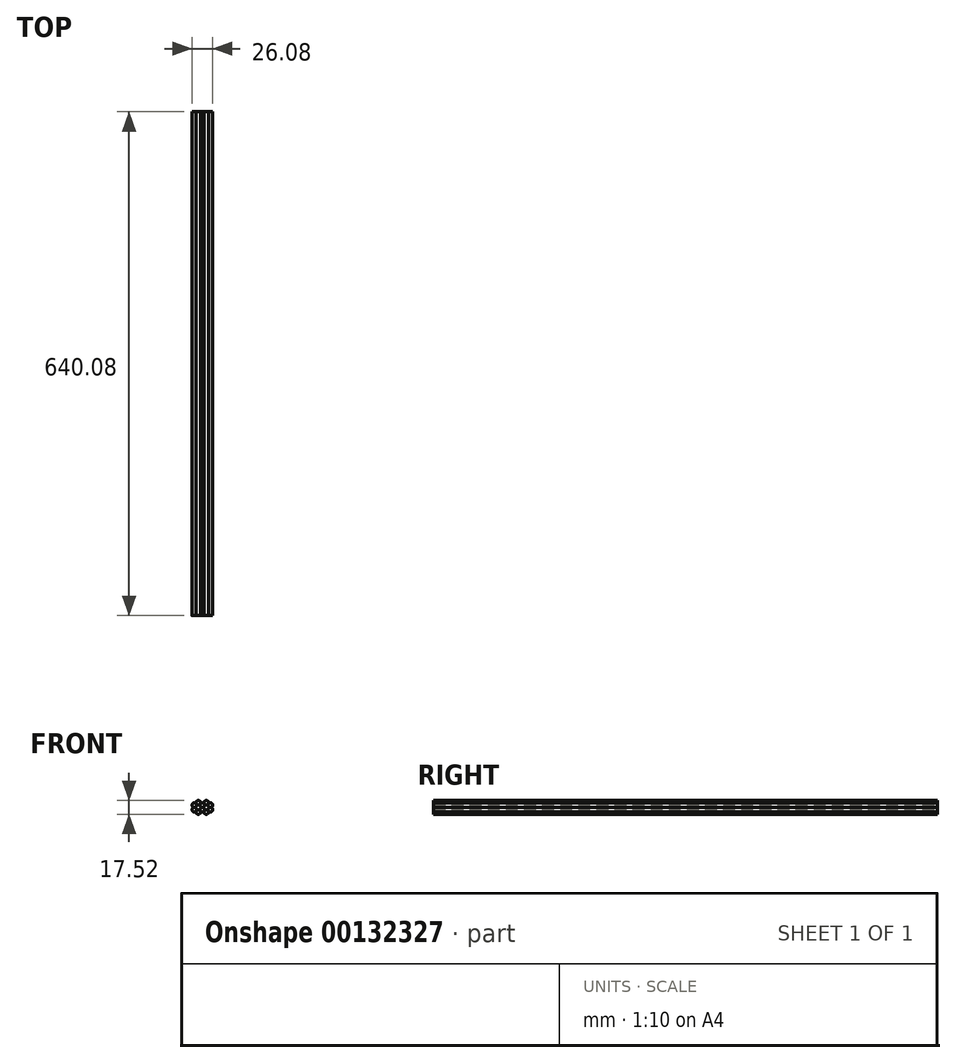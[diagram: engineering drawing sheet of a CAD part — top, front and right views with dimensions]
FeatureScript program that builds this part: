
annotation { "Feature Type Name" : "Feature", "Feature Type Description" : "" }
export const myFeature = defineFeature(function(context is Context, id is Id, definition is map)
    precondition{}
    {
        {
            var Q0;
            Q0=qCreatedBy(makeId("Front.planeOp"),FACE);
            var sketch = newSketch(context, id + "F0", { "sketchPlane" : qUnion([Q0])});
            skCircle(sketch, "E0", {"center": v(0, 0) * mm, "radius": 2.92 * mm});
            skCircle(sketch, "E1", {"center": v(-5.06, 2.92) * mm, "radius": 2.92 * mm});
            skCircle(sketch, "E2", {"center": v(-10.12, 0) * mm, "radius": 2.92 * mm});
            skCircle(sketch, "E3", {"center": v(-10.12, -5.84) * mm, "radius": 2.92 * mm});
            skCircle(sketch, "E4", {"center": v(-5.06, -8.76) * mm, "radius": 2.92 * mm});
            skCircle(sketch, "E5", {"center": v(5.06, 2.92) * mm, "radius": 2.92 * mm});
            skCircle(sketch, "E6", {"center": v(10.12, 0) * mm, "radius": 2.92 * mm});
            skCircle(sketch, "E7", {"center": v(10.12, -5.84) * mm, "radius": 2.92 * mm});
            skCircle(sketch, "E8", {"center": v(5.06, -8.76) * mm, "radius": 2.92 * mm});
            skCircle(sketch, "E9", {"center": v(0, -5.84) * mm, "radius": 2.92 * mm});
            skSolve(sketch);
        }
        {
            var Q0;
            {var subQ0=sQuery(id+"F0.wireOp",EDGE,"E8");var subQ1=makeQuery(id+"F0.imprint","INTERSECT",VERTEX,{"derivedFrom":[sQuery(id+"F0.wireOp",EDGE,"E7"),subQ0]});Q0=makeQuery(id+"F0.imprint","IMPRINT",FACE,{"disambiguationData":[TD([[makeQuery(id+"F0.imprint","IMPRINT",EDGE,{"disambiguationData":[TD([[subQ1,-1.0]])],"derivedFrom":subQ0}),1.0]])]});}
            var Q1;
            {var subQ0=sQuery(id+"F0.wireOp",EDGE,"E0");var subQ1=makeQuery(id+"F0.imprint","INTERSECT",VERTEX,{"derivedFrom":[subQ0,sQuery(id+"F0.wireOp",EDGE,"E1")]});Q1=makeQuery(id+"F0.imprint","IMPRINT",FACE,{"disambiguationData":[TD([[makeQuery(id+"F0.imprint","IMPRINT",EDGE,{"disambiguationData":[TD([[subQ1,1.0]])],"derivedFrom":subQ0}),1.0]])]});}
            var Q2;
            {var subQ0=sQuery(id+"F0.wireOp",EDGE,"E7");var subQ1=makeQuery(id+"F0.imprint","INTERSECT",VERTEX,{"derivedFrom":[sQuery(id+"F0.wireOp",EDGE,"E6"),subQ0]});Q2=makeQuery(id+"F0.imprint","IMPRINT",FACE,{"disambiguationData":[TD([[makeQuery(id+"F0.imprint","IMPRINT",EDGE,{"disambiguationData":[TD([[subQ1,-1.0]])],"derivedFrom":subQ0}),1.0]])]});}
            var Q3;
            {var subQ0=sQuery(id+"F0.wireOp",EDGE,"E4");var subQ1=makeQuery(id+"F0.imprint","INTERSECT",VERTEX,{"derivedFrom":[sQuery(id+"F0.wireOp",EDGE,"E3"),subQ0]});Q3=makeQuery(id+"F0.imprint","IMPRINT",FACE,{"disambiguationData":[TD([[makeQuery(id+"F0.imprint","IMPRINT",EDGE,{"disambiguationData":[TD([[subQ1,1.0]])],"derivedFrom":subQ0}),1.0]])]});}
            var Q4;
            {var subQ0=sQuery(id+"F0.wireOp",EDGE,"E6");var subQ1=makeQuery(id+"F0.imprint","INTERSECT",VERTEX,{"derivedFrom":[sQuery(id+"F0.wireOp",EDGE,"E5"),subQ0]});Q4=makeQuery(id+"F0.imprint","IMPRINT",FACE,{"disambiguationData":[TD([[makeQuery(id+"F0.imprint","IMPRINT",EDGE,{"disambiguationData":[TD([[subQ1,-1.0]])],"derivedFrom":subQ0}),1.0]])]});}
            var Q5;
            {var subQ0=sQuery(id+"F0.wireOp",EDGE,"E5");var subQ1=makeQuery(id+"F0.imprint","INTERSECT",VERTEX,{"derivedFrom":[sQuery(id+"F0.wireOp",EDGE,"E0"),subQ0]});Q5=makeQuery(id+"F0.imprint","IMPRINT",FACE,{"disambiguationData":[TD([[makeQuery(id+"F0.imprint","IMPRINT",EDGE,{"disambiguationData":[TD([[subQ1,-1.0]])],"derivedFrom":subQ0}),1.0]])]});}
            var Q6;
            {var subQ0=sQuery(id+"F0.wireOp",EDGE,"E1");var subQ1=makeQuery(id+"F0.imprint","INTERSECT",VERTEX,{"derivedFrom":[sQuery(id+"F0.wireOp",EDGE,"E0"),subQ0]});Q6=makeQuery(id+"F0.imprint","IMPRINT",FACE,{"disambiguationData":[TD([[makeQuery(id+"F0.imprint","IMPRINT",EDGE,{"disambiguationData":[TD([[subQ1,1.0]])],"derivedFrom":subQ0}),1.0]])]});}
            var Q7;
            {var subQ0=sQuery(id+"F0.wireOp",EDGE,"E2");var subQ1=makeQuery(id+"F0.imprint","INTERSECT",VERTEX,{"derivedFrom":[sQuery(id+"F0.wireOp",EDGE,"E1"),subQ0]});Q7=makeQuery(id+"F0.imprint","IMPRINT",FACE,{"disambiguationData":[TD([[makeQuery(id+"F0.imprint","IMPRINT",EDGE,{"disambiguationData":[TD([[subQ1,-1.0]])],"derivedFrom":subQ0}),1.0]])]});}
            var Q8;
            {var subQ0=sQuery(id+"F0.wireOp",EDGE,"E3");var subQ1=makeQuery(id+"F0.imprint","INTERSECT",VERTEX,{"derivedFrom":[sQuery(id+"F0.wireOp",EDGE,"E2"),subQ0]});Q8=makeQuery(id+"F0.imprint","IMPRINT",FACE,{"disambiguationData":[TD([[makeQuery(id+"F0.imprint","IMPRINT",EDGE,{"disambiguationData":[TD([[subQ1,-1.0]])],"derivedFrom":subQ0}),1.0]])]});}
            var Q9;
            {var subQ0=sQuery(id+"F0.wireOp",EDGE,"E9");var subQ1=makeQuery(id+"F0.imprint","INTERSECT",VERTEX,{"derivedFrom":[sQuery(id+"F0.wireOp",EDGE,"E8"),subQ0]});Q9=makeQuery(id+"F0.imprint","IMPRINT",FACE,{"disambiguationData":[TD([[makeQuery(id+"F0.imprint","IMPRINT",EDGE,{"disambiguationData":[TD([[subQ1,-1.0]])],"derivedFrom":subQ0}),1.0]])]});}
            extrude(context, id + "F1", {"entities" : qUnion([Q0, Q1, Q2, Q3, Q4, Q5, Q6, Q7, Q8, Q9]), "depth" : 640.08 * mm});
        }
    });
